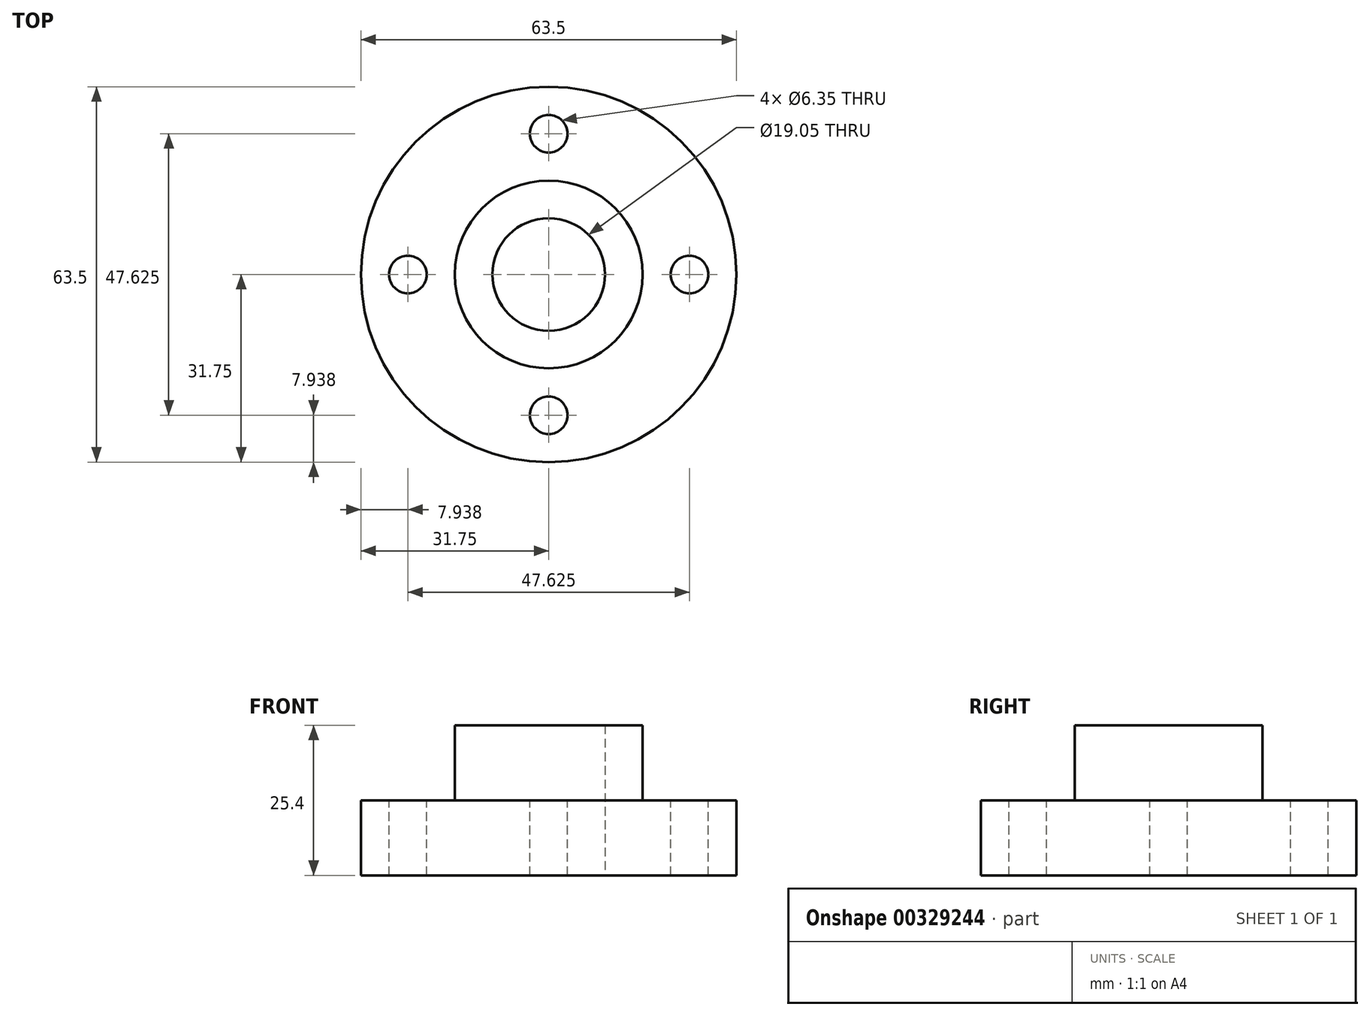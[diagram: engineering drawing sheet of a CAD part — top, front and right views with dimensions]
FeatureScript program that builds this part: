
annotation { "Feature Type Name" : "Feature", "Feature Type Description" : "" }
export const myFeature = defineFeature(function(context is Context, id is Id, definition is map)
    precondition{}
    {
        {
            var Q0;
            Q0=qCreatedBy(makeId("Top.planeOp"),FACE);
            var sketch = newSketch(context, id + "F0", { "sketchPlane" : qUnion([Q0])});
            skCircle(sketch, "E0", {"center": v(0, 0) * mm, "radius": 15.88 * mm});
            skCircle(sketch, "E1", {"center": v(0, 0) * mm, "radius": 9.53 * mm});
            skSolve(sketch);
        }
        {
            var Q0;
            Q0 = qSketchRegion(id + "F0", true);
            extrude(context, id + "F1", {"entities" : qUnion([Q0]), "depth" : 12.7 * mm});
        }
        {
            var Q0;
            Q0=makeQuery(id+"F1.opExtrude","CAP_FACE",FACE,{"disambiguationData":[OSD([sQuery(id+"F0.wireOp",EDGE,"E0"),sQuery(id+"F0.wireOp",EDGE,"E1")])],"isStart":true});
            var sketch = newSketch(context, id + "F2", { "sketchPlane" : qUnion([Q0])});
            skCircle(sketch, "E2", {"center": v(0, 0) * mm, "radius": 9.53 * mm});
            skCircle(sketch, "E3", {"center": v(0, 0) * mm, "radius": 31.75 * mm});
            skSolve(sketch);
        }
        {
            var Q0;
            Q0 = qSketchRegion(id + "F2", true);
            extrude(context, id + "F3", {"entities" : qUnion([Q0]), "operationType" : NewBodyOperationType.ADD, "depth" : 12.7 * mm});
        }
        {
            var Q0;
            Q0=makeQuery(id+"F3.opExtrude","CAP_FACE",FACE,{"disambiguationData":[OSD([sQuery(id+"F2.wireOp",EDGE,"E2"),sQuery(id+"F2.wireOp",EDGE,"E3")])],"isStart":true});
            var sketch = newSketch(context, id + "F4", { "sketchPlane" : qUnion([Q0])});
            skCircle(sketch, "E4", {"center": v(0, 23.81) * mm, "radius": 3.18 * mm});
            skCircle(sketch, "E5", {"center": v(23.81, 0) * mm, "radius": 3.18 * mm});
            skCircle(sketch, "E6", {"center": v(0, -23.81) * mm, "radius": 3.18 * mm});
            skCircle(sketch, "E7", {"center": v(-23.81, 0) * mm, "radius": 3.18 * mm});
            skLineSegment(sketch, "E8", {"start": v(0, 31.75) * mm, "end": v(0, 15.88) * mm, "construction": true});
            skLineSegment(sketch, "E9", {"start": v(-15.88, 0) * mm, "end": v(-31.75, 0) * mm, "construction": true});
            skLineSegment(sketch, "E10", {"start": v(0, -15.88) * mm, "end": v(0, -31.75) * mm, "construction": true});
            skLineSegment(sketch, "E11", {"start": v(15.88, 0) * mm, "end": v(31.75, 0) * mm, "construction": true});
            skSolve(sketch);
        }
        {
            var Q0;
            Q0=sQuery(id+"F4.wireOp",VERTEX,"E4.center");
            var Q1;
            Q1=sQuery(id+"F4.wireOp",VERTEX,"E5.center");
            var Q2;
            Q2=sQuery(id+"F4.wireOp",VERTEX,"E6.center");
            var Q3;
            Q3=sQuery(id+"F4.wireOp",VERTEX,"E7.center");
            var Q4;
            Q4=makeQuery(id+"F1.opExtrude","SWEPT_BODY",BODY,{"disambiguationData":[OSD([sQuery(id+"F0.wireOp",EDGE,"E0"),sQuery(id+"F0.wireOp",EDGE,"E1")])]});
            hole(context, id + "F5", {"style" : HoleStyle.SIMPLE, "endStyle" : HoleEndStyle.THROUGH, "holeDiameter" : 6.35 * mm, "tappedDepth" : 12.7 * mm, "tapClearance" : 3, "locations" : qUnion([Q0, Q1, Q2, Q3]), "scope" : qUnion([Q4])});
        }
    });
